# Revit family: BRG-SNT-LVD- LAVADERO DE CONCRETO
name_source: partatom
category: Aparatos sanitarios
units: mm (PartAtom-declared; Revit-internal decimal feet)

## family parameters
Compartido = Sí
Corte con vacíos al cargar = No
Cota de conector redondo = Diámetro de uso
Número OmniClass = 23.45.00.00
Punto de cálculo de habitación = Sí
Se basa en plano de trabajo = No
Siempre vertical = Sí
Tipo de pieza = Normal
Título OmniClass = Sanitary, Laundry, and Cleaning Equipment

## types (1)
- BELA MONOMANDO PARA LAVAMANOS CROMO
    Conexión AC = Sí
    Conexión AF = Sí
    Conexión de residuos = Sí
    Conexión de ventilación = Sí
    Elevación por defecto = 0 m
    Fabricante = EDESA Ecuador
    Imagen de tipo = <Ninguno>
    Modelo = 00
    URL = https://www.edesa.com.ec
    _ALT_Basamento = 0.85 m
    _ALT_Eje instalación = 0.6 m
    _EDESA_ Alto en cm = 26.2
    _EDESA_ Ancho en cm = 46.1
    _EDESA_ Consumo/capacidad de agua en L = 9.4 litros
    _EDESA_ Descripción = Fregadero de concreto
    _EDESA_ Marca = EDESA
    _EDESA_ Nombre = LAVADERO DE CONCRETO
    _EDESA_ Peso en kg = 33.1 kg
    _EDESA_ Productos necesarios para instalación = Grifería, desagüe 1 1/4", Sifón 1 1/4"
    _EDESA_ Profundidad en cm = 61.1
    _EDESA_ Página web = 0
    _EDESA_ Tipo de Aro = 0
    _EDESA_ Tipo de instalación = Sobre base de manpostería
    _EDESA_ Tolerancia dimensional = 0 m
    _EDESA_Categoria = Productos>Sanitarios>Institucional
    _EDESA_Color = Gris
    _EDESA_Conexion Hidraulica = Entrada de agua: tubería ø 1/2" Salida de agua: Tubería PVC 50
    _EDESA_Garantia = De por vida en funcionamiento y acabado del material
    _EDESA_Material = Hormigón
    _EDESA_Sku/código = SC0021500001CG
